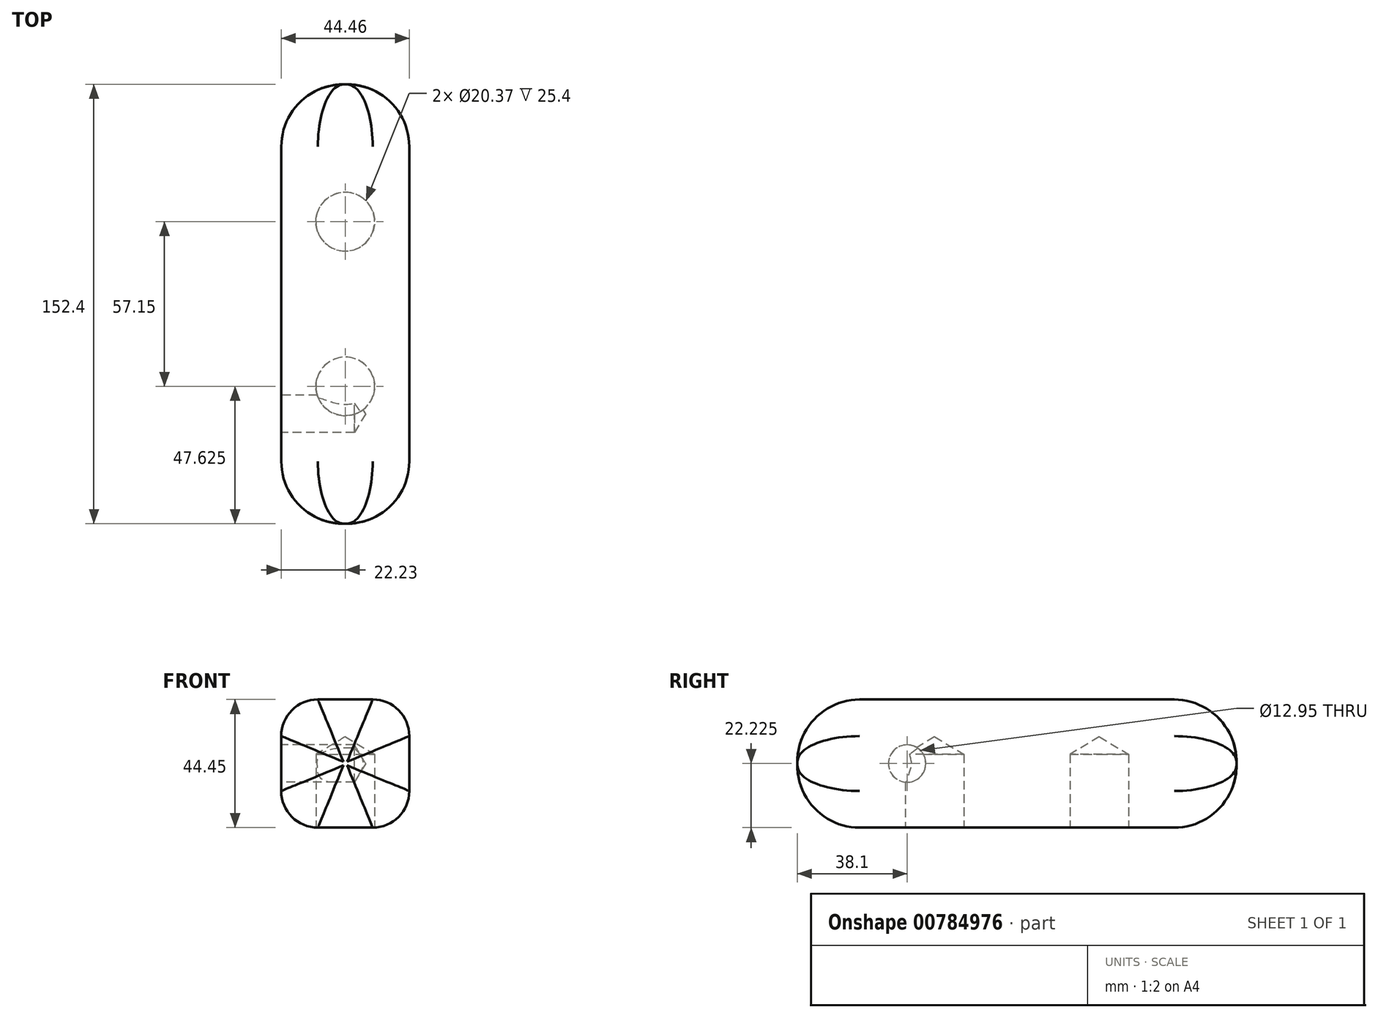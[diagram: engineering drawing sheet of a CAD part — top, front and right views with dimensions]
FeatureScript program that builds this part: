
annotation { "Feature Type Name" : "Feature", "Feature Type Description" : "" }
export const myFeature = defineFeature(function(context is Context, id is Id, definition is map)
    precondition{}
    {
        {
            var Q0;
            Q0=qCreatedBy(makeId("Top.planeOp"),FACE);
            var sketch = newSketch(context, id + "F0", { "sketchPlane" : qUnion([Q0])});
            skLineSegment(sketch, "E0.bottom", {"start": v(22.23, 76.2) * mm, "end": v(-22.22, 76.2) * mm});
            skLineSegment(sketch, "E0.top", {"start": v(22.22, -76.2) * mm, "end": v(-22.23, -76.2) * mm});
            skLineSegment(sketch, "E0.left", {"start": v(22.23, 76.2) * mm, "end": v(22.22, -76.2) * mm});
            skLineSegment(sketch, "E0.right", {"start": v(-22.22, 76.2) * mm, "end": v(-22.23, -76.2) * mm});
            skPoint(sketch, "E0.middle", {"position": v(0, 0) * mm});
            skSolve(sketch);
        }
        {
            var Q0;
            Q0 = qSketchRegion(id + "F0", true);
            extrude(context, id + "F1", {"entities" : qUnion([Q0]), "depth" : 44.45 * mm, "offsetDistance" : 25.4 * mm});
        }
        {
            var Q0;
            Q0=makeQuery(id+"F1.opExtrude","SWEPT_FACE",FACE,{"disambiguationData":[OSD([sQuery(id+"F0.wireOp",EDGE,"E0.right")])]});
            var sketch = newSketch(context, id + "F2", { "sketchPlane" : qUnion([Q0])});
            skLineSegment(sketch, "E1", {"start": v(-57.15, 22.23) * mm, "end": v(57.15, 22.23) * mm, "construction": true});
            skLineSegment(sketch, "E2", {"start": v(57.15, 22.23) * mm, "end": v(76.2, 22.23) * mm, "construction": true});
            skLineSegment(sketch, "E3", {"start": v(-57.15, 22.23) * mm, "end": v(-76.2, 22.23) * mm, "construction": true});
            skLineSegment(sketch, "E4", {"start": v(-76.2, 22.23) * mm, "end": v(-76.2, 36.4) * mm, "construction": true});
            skLineSegment(sketch, "E5", {"start": v(-76.2, 36.4) * mm, "end": v(38.1, 36.4) * mm, "construction": true});
            skLineSegment(sketch, "E6", {"start": v(38.1, 36.4) * mm, "end": v(38.1, 22.23) * mm, "construction": true});
            skPoint(sketch, "E7", {"position": v(38.1, 22.23) * mm});
            skSolve(sketch);
        }
        {
            var Q0;
            Q0=sQuery(id+"F2.wireOp",VERTEX,"E7");
            var Q1;
            Q1=makeQuery(id+"F1.opExtrude","SWEPT_BODY",BODY,{"disambiguationData":[OSD([sQuery(id+"F0.wireOp",EDGE,"E0.bottom"),sQuery(id+"F0.wireOp",EDGE,"E0.top"),sQuery(id+"F0.wireOp",EDGE,"E0.left"),sQuery(id+"F0.wireOp",EDGE,"E0.right")])]});
            hole(context, id + "F3", {"style" : HoleStyle.SIMPLE, "endStyle" : HoleEndStyle.BLIND, "holeDiameter" : 12.95 * mm, "majorDiameter" : 6.35 * mm, "holeDepth" : 25.4 * mm, "isTappedThrough" : true, "tappedDepth" : 12.7 * mm, "tapClearance" : 3, "startFromSketch" : true, "locations" : qUnion([Q0]), "scope" : qUnion([Q1])});
        }
        {
            var Q0;
            Q0=makeQuery(id+"F1.opExtrude","CAP_FACE",FACE,{"disambiguationData":[OSD([sQuery(id+"F0.wireOp",EDGE,"E0.bottom"),sQuery(id+"F0.wireOp",EDGE,"E0.top"),sQuery(id+"F0.wireOp",EDGE,"E0.left"),sQuery(id+"F0.wireOp",EDGE,"E0.right")])],"isStart":true});
            var sketch = newSketch(context, id + "F4", { "sketchPlane" : qUnion([Q0])});
            skLineSegment(sketch, "E8", {"start": v(0, 57.15) * mm, "end": v(0, 0) * mm, "construction": true});
            skLineSegment(sketch, "E9", {"start": v(0, 0) * mm, "end": v(0, -57.15) * mm, "construction": true});
            skPoint(sketch, "E10", {"position": v(0, 28.58) * mm});
            skPoint(sketch, "E11", {"position": v(0, -28.58) * mm});
            skSolve(sketch);
        }
        {
            var Q0;
            Q0=sQuery(id+"F4.wireOp",VERTEX,"E10");
            var Q1;
            Q1=makeQuery(id+"F1.opExtrude","SWEPT_BODY",BODY,{"disambiguationData":[OSD([sQuery(id+"F0.wireOp",EDGE,"E0.bottom"),sQuery(id+"F0.wireOp",EDGE,"E0.top"),sQuery(id+"F0.wireOp",EDGE,"E0.left"),sQuery(id+"F0.wireOp",EDGE,"E0.right")])]});
            hole(context, id + "F5", {"style" : HoleStyle.SIMPLE, "endStyle" : HoleEndStyle.BLIND, "holeDiameter" : 20.37 * mm, "majorDiameter" : 6.35 * mm, "holeDepth" : 25.4 * mm, "isTappedThrough" : true, "tappedDepth" : 12.7 * mm, "tapClearance" : 3, "startFromSketch" : true, "locations" : qUnion([Q0]), "scope" : qUnion([Q1])});
        }
        {
            var Q0;
            Q0=sQuery(id+"F4.wireOp",VERTEX,"E11");
            var Q1;
            Q1=makeQuery(id+"F1.opExtrude","SWEPT_BODY",BODY,{"disambiguationData":[OSD([sQuery(id+"F0.wireOp",EDGE,"E0.bottom"),sQuery(id+"F0.wireOp",EDGE,"E0.top"),sQuery(id+"F0.wireOp",EDGE,"E0.left"),sQuery(id+"F0.wireOp",EDGE,"E0.right")])]});
            hole(context, id + "F6", {"style" : HoleStyle.SIMPLE, "endStyle" : HoleEndStyle.BLIND, "holeDiameter" : 20.37 * mm, "majorDiameter" : 6.35 * mm, "holeDepth" : 25.4 * mm, "isTappedThrough" : true, "tappedDepth" : 12.7 * mm, "tapClearance" : 3, "startFromSketch" : true, "locations" : qUnion([Q0]), "scope" : qUnion([Q1])});
        }
        {
            var Q0;
            Q0=makeQuery(id+"F1.opExtrude","SWEPT_EDGE",EDGE,{"disambiguationData":[OSD([sQuery(id+"F0.wireOp",EDGE,"E0.top"),sQuery(id+"F0.wireOp",EDGE,"E0.right")])]});
            var Q1;
            Q1=makeQuery(id+"F1.opExtrude","CAP_EDGE",EDGE,{"disambiguationData":[OSD([sQuery(id+"F0.wireOp",EDGE,"E0.top")])],"isStart":true});
            var Q2;
            Q2=makeQuery(id+"F1.opExtrude","SWEPT_EDGE",EDGE,{"disambiguationData":[OSD([sQuery(id+"F0.wireOp",EDGE,"E0.top"),sQuery(id+"F0.wireOp",EDGE,"E0.left")])]});
            var Q3;
            Q3=makeQuery(id+"F1.opExtrude","CAP_EDGE",EDGE,{"disambiguationData":[OSD([sQuery(id+"F0.wireOp",EDGE,"E0.top")])],"isStart":false});
            fillet(context, id + "F7", {"entities" : qUnion([Q0, Q1, Q2, Q3]), "radius" : 21.59 * mm, "tangentPropagation" : true, "allowEdgeOverflow" : false});
        }
        {
            var Q0;
            Q0=makeQuery(id+"F1.opExtrude","CAP_EDGE",EDGE,{"disambiguationData":[OSD([sQuery(id+"F0.wireOp",EDGE,"E0.right")])],"isStart":true});
            var Q1;
            Q1=makeQuery(id+"F1.opExtrude","CAP_EDGE",EDGE,{"disambiguationData":[OSD([sQuery(id+"F0.wireOp",EDGE,"E0.right")])],"isStart":false});
            var Q2;
            Q2=makeQuery(id+"F1.opExtrude","CAP_EDGE",EDGE,{"disambiguationData":[OSD([sQuery(id+"F0.wireOp",EDGE,"E0.left")])],"isStart":true});
            var Q3;
            Q3=makeQuery(id+"F1.opExtrude","CAP_EDGE",EDGE,{"disambiguationData":[OSD([sQuery(id+"F0.wireOp",EDGE,"E0.left")])],"isStart":false});
            fillet(context, id + "F8", {"entities" : qUnion([Q0, Q1, Q2, Q3]), "radius" : 12.7 * mm, "tangentPropagation" : true, "allowEdgeOverflow" : false});
        }
        {
            var Q0;
            Q0=makeQuery(id+"F1.opExtrude","CAP_EDGE",EDGE,{"disambiguationData":[OSD([sQuery(id+"F0.wireOp",EDGE,"E0.bottom")])],"isStart":true});
            var Q1;
            Q1=makeQuery(id+"F1.opExtrude","SWEPT_EDGE",EDGE,{"disambiguationData":[OSD([sQuery(id+"F0.wireOp",EDGE,"E0.bottom"),sQuery(id+"F0.wireOp",EDGE,"E0.left")])]});
            var Q2;
            Q2=makeQuery(id+"F1.opExtrude","CAP_EDGE",EDGE,{"disambiguationData":[OSD([sQuery(id+"F0.wireOp",EDGE,"E0.bottom")])],"isStart":false});
            var Q3;
            Q3=makeQuery(id+"F1.opExtrude","SWEPT_EDGE",EDGE,{"disambiguationData":[OSD([sQuery(id+"F0.wireOp",EDGE,"E0.bottom"),sQuery(id+"F0.wireOp",EDGE,"E0.right")])]});
            fillet(context, id + "F9", {"entities" : qUnion([Q0, Q1, Q2, Q3]), "radius" : 21.59 * mm, "tangentPropagation" : true, "allowEdgeOverflow" : false});
        }
    });
